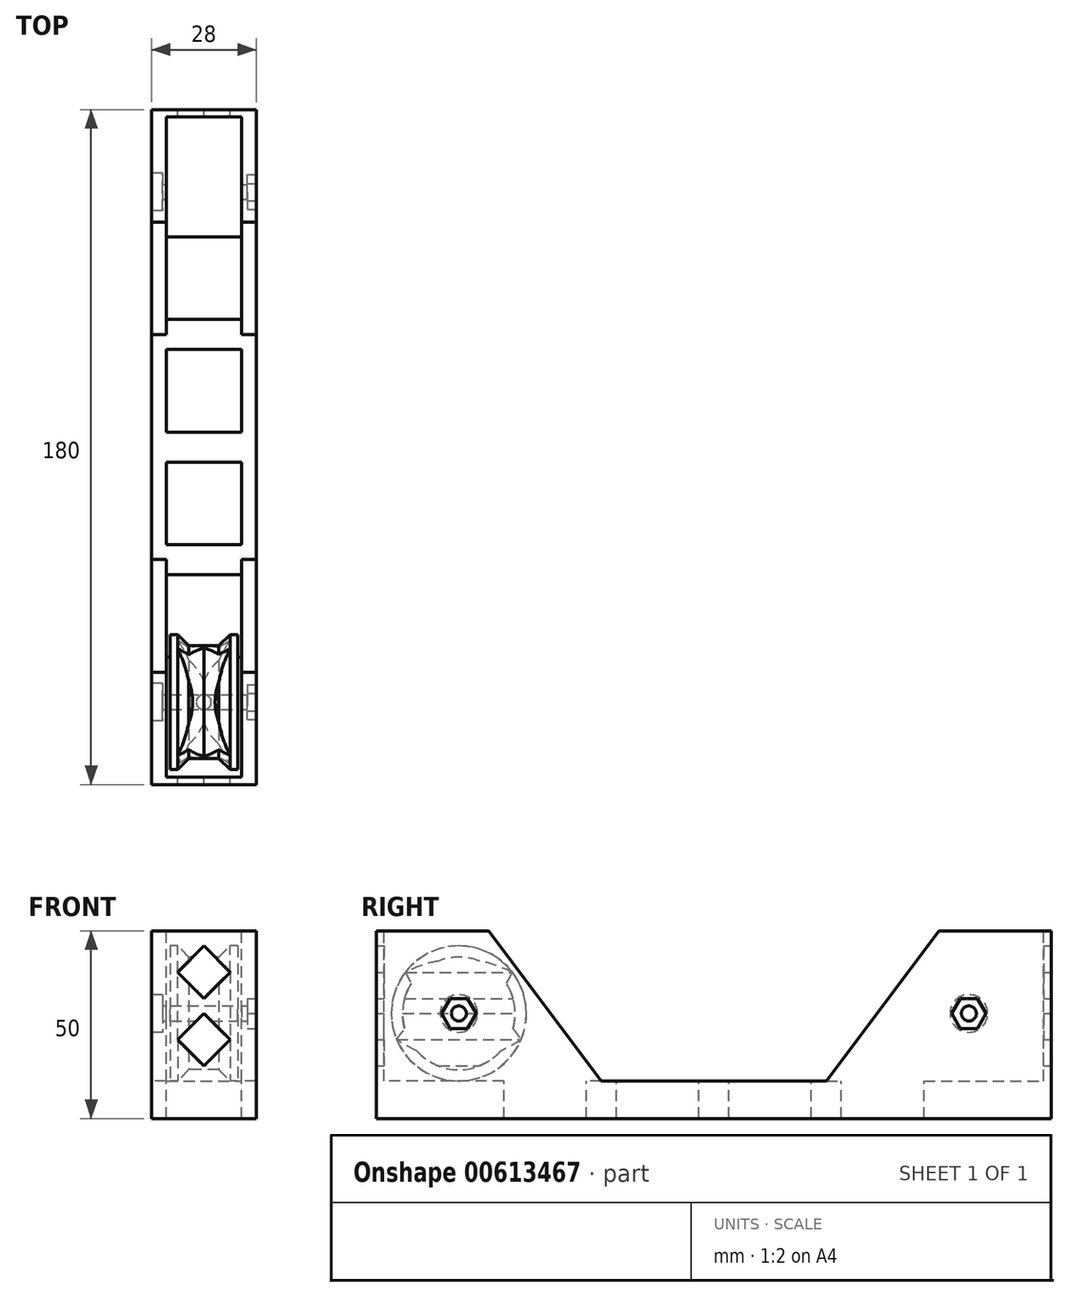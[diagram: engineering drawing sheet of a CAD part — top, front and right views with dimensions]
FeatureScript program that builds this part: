
annotation { "Feature Type Name" : "Feature", "Feature Type Description" : "" }
export const myFeature = defineFeature(function(context is Context, id is Id, definition is map)
    precondition{}
    {
        {
            var Q0;
            Q0=qCreatedBy(makeId("Right.planeOp"),FACE);
            var sketch = newSketch(context, id + "F0", { "sketchPlane" : qUnion([Q0])});
            skLineSegment(sketch, "E0", {"start": v(0, 0) * mm, "end": v(-90, 0) * mm});
            skLineSegment(sketch, "E1", {"start": v(-90, 0) * mm, "end": v(-90, 50) * mm});
            skLineSegment(sketch, "E2", {"start": v(-90, 50) * mm, "end": v(-60, 50) * mm});
            skLineSegment(sketch, "E3", {"start": v(-60, 50) * mm, "end": v(-30, 10) * mm});
            skLineSegment(sketch, "E4", {"start": v(-30, 10) * mm, "end": v(0, 10) * mm});
            skLineSegment(sketch, "E5.MirrorCS", {"start": v(30, 10) * mm, "end": v(0, 10) * mm});
            skLineSegment(sketch, "E6.MirrorCS", {"start": v(0, 0) * mm, "end": v(90, 0) * mm});
            skLineSegment(sketch, "E7.MirrorCS", {"start": v(90, 0) * mm, "end": v(90, 50) * mm});
            skLineSegment(sketch, "E8.MirrorCS", {"start": v(90, 50) * mm, "end": v(60, 50) * mm});
            skLineSegment(sketch, "E9.MirrorCS", {"start": v(60, 50) * mm, "end": v(30, 10) * mm});
            skPoint(sketch, "E10", {"position": v(-68, 28) * mm});
            skLineSegment(sketch, "E11", {"start": v(-68, 50) * mm, "end": v(-68, 0) * mm, "construction": true});
            skPoint(sketch, "E12.MirrorP", {"position": v(68, 28) * mm});
            skCircle(sketch, "E13", {"center": v(0, 120.74) * mm, "radius": 100 * mm, "construction": true});
            skCircle(sketch, "E14", {"center": v(-68, 28) * mm, "radius": 15 * mm});
            skSolve(sketch);
        }
        {
            var Q0;
            Q0=makeQuery(id+"F0.imprint","IMPRINT",FACE,{"disambiguationData":[TD([[makeQuery(id+"F0.imprint","IMPRINT",EDGE,{"derivedFrom":sQuery(id+"F0.wireOp",EDGE,"E0")}),-1.0]])]});
            var Q1;
            Q1=makeQuery(id+"F0.imprint","IMPRINT",FACE,{"disambiguationData":[TD([[makeQuery(id+"F0.imprint","IMPRINT",EDGE,{"derivedFrom":sQuery(id+"F0.wireOp",EDGE,"E14")}),1.0]])]});
            extrude(context, id + "F1", {"entities" : qUnion([Q0, Q1]), "endBound" : BoundingType.SYMMETRIC, "depth" : 28 * mm, "offsetDistance" : 25 * mm});
        }
        {
            var Q0;
            Q0=makeQuery(id+"F1.opExtrude","SWEPT_FACE",FACE,{"disambiguationData":[OSD([sQuery(id+"F0.wireOp",EDGE,"E2")])]});
            var sketch = newSketch(context, id + "F2", { "sketchPlane" : qUnion([Q0])});
            skLineSegment(sketch, "E15", {"start": v(-10, -30) * mm, "end": v(-10, -88) * mm});
            skLineSegment(sketch, "E16.MirrorCS", {"start": v(10, -30) * mm, "end": v(10, -88) * mm});
            skLineSegment(sketch, "E17.MirrorCS", {"start": v(10, 30) * mm, "end": v(10, 88) * mm});
            skLineSegment(sketch, "E18.MirrorCS", {"start": v(-10, 30) * mm, "end": v(-10, 88) * mm});
            skLineSegment(sketch, "E19", {"start": v(-10, -30) * mm, "end": v(10, -30) * mm});
            skLineSegment(sketch, "E20", {"start": v(-10, -88) * mm, "end": v(-11, -88) * mm});
            skLineSegment(sketch, "E21.MirrorCS", {"start": v(-10, 30) * mm, "end": v(10, 30) * mm});
            skLineSegment(sketch, "E22.MirrorCS", {"start": v(-11, 88) * mm, "end": v(-10, 88) * mm});
            skLineSegment(sketch, "E23", {"start": v(-10, -88) * mm, "end": v(10, -88) * mm});
            skLineSegment(sketch, "E24.MirrorCS", {"start": v(-10, 88) * mm, "end": v(10, 88) * mm});
            skSolve(sketch);
        }
        {
            var Q0;
            {var subQ0=sQuery(id+"F2.wireOp",EDGE,"E19");Q0=makeQuery(id+"F2.imprint","IMPRINT",FACE,{"disambiguationData":[TD([[makeQuery(id+"F2.imprint","IMPRINT",EDGE,{"derivedFrom":subQ0}),-1.0]])]});}
            var Q1;
            {var subQ0=sQuery(id+"F2.wireOp",EDGE,"E20");Q1=makeQuery(id+"F2.imprint","IMPRINT",FACE,{"disambiguationData":[TD([[makeQuery(id+"F2.imprint","IMPRINT",EDGE,{"derivedFrom":subQ0}),-1.0]])]});}
            var Q2;
            Q2=makeQuery(id+"F1.opExtrude","SWEPT_FACE",FACE,{"disambiguationData":[OSD([sQuery(id+"F0.wireOp",EDGE,"E0"),sQuery(id+"F0.wireOp",EDGE,"E6.MirrorCS")])]});
            extrude(context, id + "F3", {"entities" : qUnion([Q0, Q1]), "operationType" : NewBodyOperationType.REMOVE, "endBound" : BoundingType.UP_TO_SURFACE, "oppositeDirection" : true, "depth" : 25 * mm, "endBoundEntityFace" : qUnion([Q2]), "hasOffset" : true, "offsetDistance" : 10 * mm});
        }
        {
            var Q0;
            Q0=makeQuery(id+"F2.imprint","IMPRINT",FACE,{"disambiguationData":[TD([[makeQuery(id+"F2.imprint","IMPRINT",EDGE,{"derivedFrom":sQuery(id+"F2.wireOp",EDGE,"E17.MirrorCS")}),1.0]])]});
            var Q1;
            {var subQ0=sQuery(id+"F2.wireOp",EDGE,"E23");Q1=makeQuery(id+"F2.imprint","IMPRINT",FACE,{"disambiguationData":[TD([[makeQuery(id+"F2.imprint","IMPRINT",EDGE,{"derivedFrom":subQ0}),1.0]])]});}
            var Q2;
            Q2=makeQuery(id+"F1.opExtrude","SWEPT_FACE",FACE,{"disambiguationData":[OSD([sQuery(id+"F0.wireOp",EDGE,"E0"),sQuery(id+"F0.wireOp",EDGE,"E6.MirrorCS")])]});
            extrude(context, id + "F4", {"entities" : qUnion([Q0, Q1]), "operationType" : NewBodyOperationType.REMOVE, "endBound" : BoundingType.UP_TO_SURFACE, "oppositeDirection" : true, "depth" : 25 * mm, "endBoundEntityFace" : qUnion([Q2]), "hasOffset" : true, "offsetDistance" : 10 * mm});
        }
        {
            var Q0;
            Q0=sQuery(id+"F0.wireOp",VERTEX,"E10");
            var Q1;
            Q1=makeQuery(id+"F1.opExtrude","SWEPT_FACE",FACE,{"disambiguationData":[OSD([sQuery(id+"F0.wireOp",EDGE,"E1")])]});
            cPlane(context, id + "F5", {"entities" : qUnion([Q0, Q1]), "cplaneType" : CPlaneType.PLANE_POINT, "offset" : 25 * mm, "width" : 150 * mm, "height" : 150 * mm});
        }
        {
            var Q0;
            Q0=qCreatedBy(id+"F5.planeOp",FACE);
            var sketch = newSketch(context, id + "F6", { "sketchPlane" : qUnion([Q0])});
            skLineSegment(sketch, "E25.0", {"start": v(0, 43) * mm, "end": v(0, 13) * mm, "construction": true});
            skLineSegment(sketch, "E26", {"start": v(0, 43) * mm, "end": v(-4, 43) * mm});
            skLineSegment(sketch, "E27", {"start": v(-4, 43) * mm, "end": v(-7, 46) * mm});
            skLineSegment(sketch, "E28", {"start": v(-7, 46) * mm, "end": v(-9, 46) * mm});
            skLineSegment(sketch, "E29", {"start": v(-9, 46) * mm, "end": v(-9, 28) * mm});
            skPoint(sketch, "E29.endSnap0", {"position": v(0, 28) * mm});
            skLineSegment(sketch, "E30.MirrorCS", {"start": v(0, 43) * mm, "end": v(4, 43) * mm});
            skLineSegment(sketch, "E31.MirrorCS", {"start": v(4, 43) * mm, "end": v(7, 46) * mm});
            skLineSegment(sketch, "E32.MirrorCS", {"start": v(7, 46) * mm, "end": v(9, 46) * mm});
            skLineSegment(sketch, "E33.MirrorCS", {"start": v(9, 46) * mm, "end": v(9, 28) * mm});
            skLineSegment(sketch, "E34", {"start": v(-9, 28) * mm, "end": v(0, 28) * mm});
            skLineSegment(sketch, "E35.MirrorCS", {"start": v(9, 28) * mm, "end": v(0, 28) * mm});
            skSolve(sketch);
        }
        {
            var Q0;
            Q0=qSketchRegion(id+"F6",true);
            var Q1;
            Q1=sQuery(id+"F6.wireOp",EDGE,"E34");
            revolve(context, id + "F7", {"entities" : qUnion([Q0]), "axis" : qUnion([Q1]), "revolveType" : RevolveType.FULL});
        }
        {
            var Q0;
            Q0=makeQuery(id+"F1.opExtrude","CAP_FACE",FACE,{"disambiguationData":[OSD([sQuery(id+"F0.wireOp",EDGE,"E0"),sQuery(id+"F0.wireOp",EDGE,"E1"),sQuery(id+"F0.wireOp",EDGE,"E2"),sQuery(id+"F0.wireOp",EDGE,"E3"),sQuery(id+"F0.wireOp",EDGE,"E4"),sQuery(id+"F0.wireOp",EDGE,"E5.MirrorCS"),sQuery(id+"F0.wireOp",EDGE,"E6.MirrorCS"),sQuery(id+"F0.wireOp",EDGE,"E7.MirrorCS"),sQuery(id+"F0.wireOp",EDGE,"E8.MirrorCS"),sQuery(id+"F0.wireOp",EDGE,"E9.MirrorCS")])],"isStart":false});
            var sketch = newSketch(context, id + "F8", { "sketchPlane" : qUnion([Q0])});
            skPoint(sketch, "E36.0", {"position": v(-68, 28) * mm});
            skPoint(sketch, "E37.0", {"position": v(68, 28) * mm});
            skCircle(sketch, "E38.cCircle", {"center": v(-68, 28) * mm, "radius": 4 * mm, "construction": true});
            skLineSegment(sketch, "E38.0", {"start": v(-65.7, 24) * mm, "end": v(-70.3, 24) * mm});
            skLineSegment(sketch, "E38.1", {"start": v(-70.3, 24) * mm, "end": v(-72.62, 28) * mm});
            skLineSegment(sketch, "E38.2", {"start": v(-72.62, 28) * mm, "end": v(-70.3, 32) * mm});
            skLineSegment(sketch, "E38.3", {"start": v(-70.3, 32) * mm, "end": v(-65.7, 32) * mm});
            skLineSegment(sketch, "E38.4", {"start": v(-65.7, 32) * mm, "end": v(-63.38, 28) * mm});
            skLineSegment(sketch, "E38.5", {"start": v(-63.38, 28) * mm, "end": v(-65.7, 24) * mm});
            skPoint(sketch, "E38.0.midPoint", {"position": v(-68, 24) * mm});
            skLineSegment(sketch, "E39.MirrorCS", {"start": v(65.7, 32) * mm, "end": v(63.38, 28) * mm});
            skLineSegment(sketch, "E40.MirrorCS", {"start": v(70.3, 32) * mm, "end": v(65.7, 32) * mm});
            skLineSegment(sketch, "E41.MirrorCS", {"start": v(72.62, 28) * mm, "end": v(70.3, 32) * mm});
            skLineSegment(sketch, "E42.MirrorCS", {"start": v(70.3, 24) * mm, "end": v(72.62, 28) * mm});
            skLineSegment(sketch, "E43.MirrorCS", {"start": v(65.7, 24) * mm, "end": v(70.3, 24) * mm});
            skLineSegment(sketch, "E44.MirrorCS", {"start": v(63.38, 28) * mm, "end": v(65.7, 24) * mm});
            skSolve(sketch);
        }
        {
            var Q0;
            Q0=sQuery(id+"F8.wireOp",VERTEX,"E36.0");
            var Q1;
            Q1=sQuery(id+"F8.wireOp",VERTEX,"E37.0");
            var Q2;
            Q2=makeQuery(id+"F1.opExtrude","SWEPT_BODY",BODY,{"disambiguationData":[OSD([sQuery(id+"F0.wireOp",EDGE,"E0"),sQuery(id+"F0.wireOp",EDGE,"E1"),sQuery(id+"F0.wireOp",EDGE,"E2"),sQuery(id+"F0.wireOp",EDGE,"E3"),sQuery(id+"F0.wireOp",EDGE,"E4"),sQuery(id+"F0.wireOp",EDGE,"E5.MirrorCS"),sQuery(id+"F0.wireOp",EDGE,"E6.MirrorCS"),sQuery(id+"F0.wireOp",EDGE,"E7.MirrorCS"),sQuery(id+"F0.wireOp",EDGE,"E8.MirrorCS"),sQuery(id+"F0.wireOp",EDGE,"E9.MirrorCS")])]});
            var Q3;
            Q3=makeQuery(id+"F7.opRevolve","SWEPT_BODY",BODY,{"disambiguationData":[OSD([sQuery(id+"F6.wireOp",EDGE,"E26"),sQuery(id+"F6.wireOp",EDGE,"E27"),sQuery(id+"F6.wireOp",EDGE,"E28"),sQuery(id+"F6.wireOp",EDGE,"E29"),sQuery(id+"F6.wireOp",EDGE,"E30.MirrorCS"),sQuery(id+"F6.wireOp",EDGE,"E31.MirrorCS"),sQuery(id+"F6.wireOp",EDGE,"E32.MirrorCS"),sQuery(id+"F6.wireOp",EDGE,"E33.MirrorCS"),sQuery(id+"F6.wireOp",EDGE,"E34"),sQuery(id+"F6.wireOp",EDGE,"E35.MirrorCS")])]});
            hole(context, id + "F9", {"style" : HoleStyle.SIMPLE, "endStyle" : HoleEndStyle.THROUGH, "holeDiameter" : 4 * mm, "isTappedThrough" : true, "tappedDepth" : 6 * mm, "tapClearance" : 3, "locations" : qUnion([Q0, Q1]), "scope" : qUnion([Q2, Q3])});
        }
        {
            var Q0;
            {var subQ0=sQuery(id+"F0.wireOp",EDGE,"E6.MirrorCS");var subQ1=sQuery(id+"F0.wireOp",EDGE,"E0");Q0=makeQuery(id+"F4.boolean.opBoolean","MERGE",FACE,{"derivedFrom":[makeQuery(id+"F3.boolean.opBoolean","MERGE",FACE,{"derivedFrom":[makeQuery(id+"F1.opExtrude","SWEPT_FACE",FACE,{"disambiguationData":[OSD([sQuery(id+"F0.wireOp",EDGE,"E4"),sQuery(id+"F0.wireOp",EDGE,"E5.MirrorCS")])]}),makeQuery(id+"F3.opExtrude","CAP_FACE",FACE,{"disambiguationData":[OSD([subQ1,subQ0])],"isStart":false})]}),makeQuery(id+"F4.opExtrude","CAP_FACE",FACE,{"disambiguationData":[OSD([subQ1,subQ0])],"isStart":false})]});}
            var sketch = newSketch(context, id + "F10", { "sketchPlane" : qUnion([Q0])});
            skPoint(sketch, "E45.middle", {"position": v(0, 0) * mm});
            skLineSegment(sketch, "E46.bottom", {"start": v(-10, 26) * mm, "end": v(10, 26) * mm});
            skLineSegment(sketch, "E46.top", {"start": v(-10, 4) * mm, "end": v(10, 4) * mm});
            skLineSegment(sketch, "E46.left", {"start": v(-10, 26) * mm, "end": v(-10, 4) * mm});
            skLineSegment(sketch, "E46.right", {"start": v(10, 26) * mm, "end": v(10, 4) * mm});
            skPoint(sketch, "E46.middle", {"position": v(0, 15) * mm});
            skLineSegment(sketch, "E47.MirrorCS", {"start": v(-10, -4) * mm, "end": v(10, -4) * mm});
            skLineSegment(sketch, "E48.MirrorCS", {"start": v(10, -26) * mm, "end": v(10, -4) * mm});
            skLineSegment(sketch, "E49.MirrorCS", {"start": v(-10, -26) * mm, "end": v(10, -26) * mm});
            skLineSegment(sketch, "E50.MirrorCS", {"start": v(-10, -26) * mm, "end": v(-10, -4) * mm});
            skLineSegment(sketch, "E51", {"start": v(14, -30) * mm, "end": v(-14, -30) * mm, "construction": true});
            skLineSegment(sketch, "E52.MirrorCS", {"start": v(-10, -34) * mm, "end": v(10, -34) * mm});
            skLineSegment(sketch, "E53.MirrorCS", {"start": v(10, -34) * mm, "end": v(10, -56) * mm});
            skLineSegment(sketch, "E54.MirrorCS", {"start": v(-10, -56) * mm, "end": v(10, -56) * mm});
            skLineSegment(sketch, "E55.MirrorCS", {"start": v(-10, -34) * mm, "end": v(-10, -56) * mm});
            skLineSegment(sketch, "E56.MirrorCS", {"start": v(-10, 34) * mm, "end": v(10, 34) * mm});
            skLineSegment(sketch, "E57.MirrorCS", {"start": v(-10, 56) * mm, "end": v(10, 56) * mm});
            skLineSegment(sketch, "E58.MirrorCS", {"start": v(10, 34) * mm, "end": v(10, 56) * mm});
            skLineSegment(sketch, "E59.MirrorCS", {"start": v(-10, 34) * mm, "end": v(-10, 56) * mm});
            skSolve(sketch);
        }
        {
            var Q0;
            Q0=qSketchRegion(id+"F10",true);
            var Q1;
            Q1=makeQuery(id+"F1.opExtrude","SWEPT_FACE",FACE,{"disambiguationData":[OSD([sQuery(id+"F0.wireOp",EDGE,"E0"),sQuery(id+"F0.wireOp",EDGE,"E6.MirrorCS")])]});
            extrude(context, id + "F11", {"entities" : qUnion([Q0]), "operationType" : NewBodyOperationType.REMOVE, "endBound" : BoundingType.UP_TO_SURFACE, "oppositeDirection" : true, "depth" : 25 * mm, "endBoundEntityFace" : qUnion([Q1]), "offsetDistance" : 25 * mm});
        }
        {
            var Q0;
            Q0=makeQuery(id+"F8.imprint","IMPRINT",FACE,{"disambiguationData":[TD([[makeQuery(id+"F8.imprint","IMPRINT",EDGE,{"derivedFrom":sQuery(id+"F8.wireOp",EDGE,"E38.0")}),-1.0]])]});
            var Q1;
            Q1=makeQuery(id+"F8.imprint","IMPRINT",FACE,{"disambiguationData":[TD([[makeQuery(id+"F8.imprint","IMPRINT",EDGE,{"derivedFrom":sQuery(id+"F8.wireOp",EDGE,"E39.MirrorCS")}),1.0]])]});
            var Q2;
            {var subQ0=sQuery(id+"F2.wireOp",EDGE,"E16.MirrorCS");Q2=makeQuery(id+"F4.boolean.opBoolean","MERGE",FACE,{"derivedFrom":[makeQuery(id+"F3.boolean.opBoolean","COPY",FACE,{"derivedFrom":makeQuery(id+"F3.opExtrude","SWEPT_FACE",FACE,{"disambiguationData":[OSD([subQ0])]})}),makeQuery(id+"F4.opExtrude","SWEPT_FACE",FACE,{"disambiguationData":[OSD([subQ0])]})]});}
            extrude(context, id + "F12", {"entities" : qUnion([Q0, Q1]), "operationType" : NewBodyOperationType.REMOVE, "endBound" : BoundingType.UP_TO_SURFACE, "oppositeDirection" : true, "depth" : 25 * mm, "endBoundEntityFace" : qUnion([Q2]), "hasOffset" : true, "offsetDistance" : 1.6 * mm});
        }
        {
            var Q0;
            Q0=makeQuery(id+"F1.opExtrude","CAP_FACE",FACE,{"disambiguationData":[OSD([sQuery(id+"F0.wireOp",EDGE,"E0"),sQuery(id+"F0.wireOp",EDGE,"E1"),sQuery(id+"F0.wireOp",EDGE,"E2"),sQuery(id+"F0.wireOp",EDGE,"E3"),sQuery(id+"F0.wireOp",EDGE,"E4"),sQuery(id+"F0.wireOp",EDGE,"E5.MirrorCS"),sQuery(id+"F0.wireOp",EDGE,"E6.MirrorCS"),sQuery(id+"F0.wireOp",EDGE,"E7.MirrorCS"),sQuery(id+"F0.wireOp",EDGE,"E8.MirrorCS"),sQuery(id+"F0.wireOp",EDGE,"E9.MirrorCS")])],"isStart":true});
            var sketch = newSketch(context, id + "F13", { "sketchPlane" : qUnion([Q0])});
            skCircle(sketch, "E60", {"center": v(68, 28) * mm, "radius": 5 * mm});
            skCircle(sketch, "E61.MirrorC", {"center": v(-68, 28) * mm, "radius": 5 * mm});
            skSolve(sketch);
        }
        {
            var Q0;
            Q0=qSketchRegion(id+"F13",true);
            extrude(context, id + "F14", {"entities" : qUnion([Q0]), "operationType" : NewBodyOperationType.REMOVE, "oppositeDirection" : true, "depth" : 3 * mm, "offsetDistance" : 25 * mm});
        }
        {
            var Q0;
            Q0=makeQuery(id+"F1.opExtrude","SWEPT_FACE",FACE,{"disambiguationData":[OSD([sQuery(id+"F0.wireOp",EDGE,"E7.MirrorCS")])]});
            var sketch = newSketch(context, id + "F15", { "sketchPlane" : qUnion([Q0])});
            skLineSegment(sketch, "E62.0", {"start": v(-10, 10) * mm, "end": v(-10, 50) * mm, "construction": true});
            skLineSegment(sketch, "E63.0", {"start": v(10, 10) * mm, "end": v(10, 50) * mm, "construction": true});
            skLineSegment(sketch, "E64", {"start": v(-10, 30) * mm, "end": v(10, 30) * mm, "construction": true});
            skLineSegment(sketch, "E65", {"start": v(0, 32) * mm, "end": v(-7, 39) * mm});
            skLineSegment(sketch, "E66", {"start": v(-7, 39) * mm, "end": v(0, 46) * mm});
            skLineSegment(sketch, "E67", {"start": v(0, 46) * mm, "end": v(7, 39) * mm});
            skLineSegment(sketch, "E68", {"start": v(7, 39) * mm, "end": v(0, 32) * mm});
            skLineSegment(sketch, "E69.MirrorCS", {"start": v(0, 28) * mm, "end": v(-7, 21) * mm});
            skLineSegment(sketch, "E70.MirrorCS", {"start": v(7, 21) * mm, "end": v(0, 28) * mm});
            skLineSegment(sketch, "E71.MirrorCS", {"start": v(0, 14) * mm, "end": v(7, 21) * mm});
            skLineSegment(sketch, "E72.MirrorCS", {"start": v(-7, 21) * mm, "end": v(0, 14) * mm});
            skSolve(sketch);
        }
        {
            var Q0;
            Q0=makeQuery(id+"F15.imprint","IMPRINT",FACE,{"disambiguationData":[TD([[makeQuery(id+"F15.imprint","IMPRINT",EDGE,{"derivedFrom":sQuery(id+"F15.wireOp",EDGE,"E65")}),-1.0]])]});
            var Q1;
            Q1=makeQuery(id+"F15.imprint","IMPRINT",FACE,{"disambiguationData":[TD([[makeQuery(id+"F15.imprint","IMPRINT",EDGE,{"derivedFrom":sQuery(id+"F15.wireOp",EDGE,"E69.MirrorCS")}),1.0]])]});
            var Q2;
            Q2=makeQuery(id+"F4.boolean.opBoolean","COPY",FACE,{"derivedFrom":makeQuery(id+"F4.opExtrude","SWEPT_FACE",FACE,{"disambiguationData":[OSD([sQuery(id+"F2.wireOp",EDGE,"E24.MirrorCS")])]})});
            extrude(context, id + "F16", {"entities" : qUnion([Q0, Q1]), "operationType" : NewBodyOperationType.REMOVE, "endBound" : BoundingType.THROUGH_ALL, "oppositeDirection" : true, "depth" : 25 * mm, "endBoundEntityFace" : qUnion([Q2]), "offsetDistance" : 25 * mm});
        }
    });
